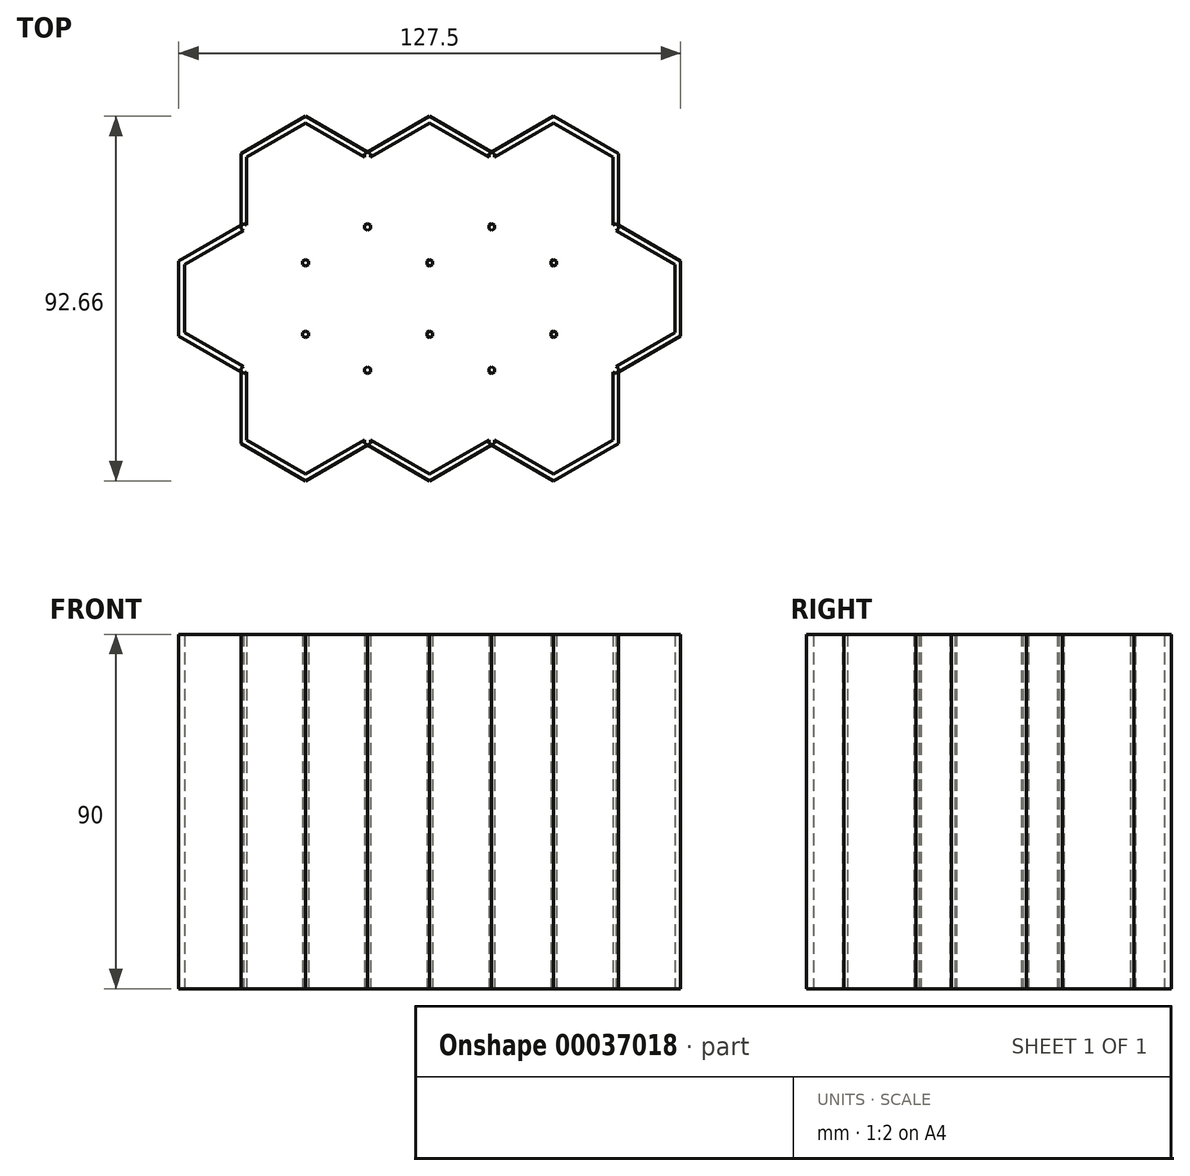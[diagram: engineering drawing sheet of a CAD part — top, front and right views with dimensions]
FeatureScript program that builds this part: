
annotation { "Feature Type Name" : "Feature", "Feature Type Description" : "" }
export const myFeature = defineFeature(function(context is Context, id is Id, definition is map)
    precondition{}
    {
        {
            var Q0;
            Q0=qCreatedBy(makeId("Top.planeOp"),FACE);
            var sketch = newSketch(context, id + "F0", { "sketchPlane" : qUnion([Q0])});
            skCircle(sketch, "E0.cCircle", {"center": v(0, 0) * mm, "radius": 15 * mm, "construction": true});
            skLineSegment(sketch, "E0.0", {"start": v(0, 17.32) * mm, "end": v(15, 8.66) * mm});
            skLineSegment(sketch, "E0.1", {"start": v(15, 8.66) * mm, "end": v(15, -8.66) * mm});
            skLineSegment(sketch, "E0.2", {"start": v(15, -8.66) * mm, "end": v(0, -17.32) * mm});
            skLineSegment(sketch, "E0.3", {"start": v(0, -17.32) * mm, "end": v(-15, -8.66) * mm});
            skLineSegment(sketch, "E0.4", {"start": v(-15, -8.66) * mm, "end": v(-15, 8.66) * mm});
            skLineSegment(sketch, "E0.5", {"start": v(-15, 8.66) * mm, "end": v(0, 17.32) * mm});
            skPoint(sketch, "E0.0.midPoint", {"position": v(7.5, 13) * mm});
            skLineSegment(sketch, "E1.0", {"start": v(-16.5, 9.53) * mm, "end": v(0, 19.05) * mm});
            skLineSegment(sketch, "E1.1", {"start": v(-16.5, -9.53) * mm, "end": v(-16.5, 9.53) * mm});
            skLineSegment(sketch, "E1.2", {"start": v(0, -19.05) * mm, "end": v(-16.5, -9.53) * mm});
            skLineSegment(sketch, "E1.3", {"start": v(16.5, -9.53) * mm, "end": v(0, -19.05) * mm});
            skLineSegment(sketch, "E1.4", {"start": v(16.5, 9.53) * mm, "end": v(16.5, -9.53) * mm});
            skLineSegment(sketch, "E1.5", {"start": v(0, 19.05) * mm, "end": v(16.5, 9.53) * mm});
            skCircle(sketch, "E2.1.0.0", {"center": v(31.5, 0) * mm, "radius": 15 * mm, "construction": true});
            skLineSegment(sketch, "E2.1.0.1", {"start": v(46.5, 8.66) * mm, "end": v(46.5, -8.66) * mm});
            skLineSegment(sketch, "E2.1.0.2", {"start": v(46.5, -8.66) * mm, "end": v(31.5, -17.32) * mm});
            skPoint(sketch, "E2.1.0.3", {"position": v(39, 13) * mm});
            skLineSegment(sketch, "E2.1.0.4", {"start": v(31.5, -19.05) * mm, "end": v(15, -9.53) * mm});
            skLineSegment(sketch, "E2.1.0.5", {"start": v(31.5, -17.32) * mm, "end": v(16.5, -8.66) * mm});
            skLineSegment(sketch, "E2.1.0.6", {"start": v(16.5, -8.66) * mm, "end": v(16.5, 8.66) * mm});
            skLineSegment(sketch, "E2.1.0.7", {"start": v(15, 9.53) * mm, "end": v(31.5, 19.05) * mm});
            skLineSegment(sketch, "E2.1.0.8", {"start": v(15, -9.53) * mm, "end": v(15, 9.53) * mm});
            skLineSegment(sketch, "E2.1.0.9", {"start": v(48, -9.53) * mm, "end": v(31.5, -19.05) * mm});
            skLineSegment(sketch, "E2.1.0.10", {"start": v(48, 9.53) * mm, "end": v(48, -9.53) * mm});
            skLineSegment(sketch, "E2.1.0.11", {"start": v(31.5, 19.05) * mm, "end": v(48, 9.53) * mm});
            skLineSegment(sketch, "E2.1.0.12", {"start": v(31.5, 17.32) * mm, "end": v(46.5, 8.66) * mm});
            skLineSegment(sketch, "E2.1.0.13", {"start": v(16.5, 8.66) * mm, "end": v(31.5, 17.32) * mm});
            skCircle(sketch, "E2.2.0.0", {"center": v(63, 0) * mm, "radius": 15 * mm, "construction": true});
            skLineSegment(sketch, "E2.2.0.1", {"start": v(78, 8.66) * mm, "end": v(78, -8.66) * mm});
            skLineSegment(sketch, "E2.2.0.2", {"start": v(78, -8.66) * mm, "end": v(63, -17.32) * mm});
            skPoint(sketch, "E2.2.0.3", {"position": v(70.5, 13) * mm});
            skLineSegment(sketch, "E2.2.0.4", {"start": v(63, -19.05) * mm, "end": v(46.5, -9.53) * mm});
            skLineSegment(sketch, "E2.2.0.5", {"start": v(63, -17.32) * mm, "end": v(48, -8.66) * mm});
            skLineSegment(sketch, "E2.2.0.6", {"start": v(48, -8.66) * mm, "end": v(48, 8.66) * mm});
            skLineSegment(sketch, "E2.2.0.7", {"start": v(46.5, 9.53) * mm, "end": v(63, 19.05) * mm});
            skLineSegment(sketch, "E2.2.0.8", {"start": v(46.5, -9.53) * mm, "end": v(46.5, 9.53) * mm});
            skLineSegment(sketch, "E2.2.0.9", {"start": v(79.5, -9.53) * mm, "end": v(63, -19.05) * mm});
            skLineSegment(sketch, "E2.2.0.10", {"start": v(79.5, 9.53) * mm, "end": v(79.5, -9.53) * mm});
            skLineSegment(sketch, "E2.2.0.11", {"start": v(63, 19.05) * mm, "end": v(79.5, 9.53) * mm});
            skLineSegment(sketch, "E2.2.0.12", {"start": v(63, 17.32) * mm, "end": v(78, 8.66) * mm});
            skLineSegment(sketch, "E2.2.0.13", {"start": v(48, 8.66) * mm, "end": v(63, 17.32) * mm});
            skLineSegment(sketch, "E2.direction1", {"start": v(0, 0) * mm, "end": v(31.5, 0) * mm, "construction": true});
            skLineSegment(sketch, "E3.1.0.0", {"start": v(-15.75, 46.33) * mm, "end": v(0.75, 36.8) * mm});
            skLineSegment(sketch, "E3.1.0.1", {"start": v(-15.75, 27.28) * mm, "end": v(15.75, 27.28) * mm, "construction": true});
            skLineSegment(sketch, "E3.1.0.2", {"start": v(-30.75, 18.62) * mm, "end": v(-30.75, 35.94) * mm});
            skLineSegment(sketch, "E3.1.0.3", {"start": v(-15.75, 9.96) * mm, "end": v(-30.75, 18.62) * mm});
            skLineSegment(sketch, "E3.1.0.4", {"start": v(-0.75, 18.62) * mm, "end": v(-15.75, 9.96) * mm});
            skLineSegment(sketch, "E3.1.0.5", {"start": v(-0.75, 35.94) * mm, "end": v(-0.75, 18.62) * mm});
            skLineSegment(sketch, "E3.1.0.6", {"start": v(0.75, 36.8) * mm, "end": v(0.75, 17.75) * mm});
            skPoint(sketch, "E3.1.0.7", {"position": v(-8.25, 40.27) * mm});
            skLineSegment(sketch, "E3.1.0.8", {"start": v(-15.75, 44.6) * mm, "end": v(-0.75, 35.94) * mm});
            skCircle(sketch, "E3.1.0.9", {"center": v(-15.75, 27.28) * mm, "radius": 15 * mm, "construction": true});
            skLineSegment(sketch, "E3.1.0.10", {"start": v(-32.25, 17.75) * mm, "end": v(-32.25, 36.8) * mm});
            skLineSegment(sketch, "E3.1.0.11", {"start": v(-15.75, 8.23) * mm, "end": v(-32.25, 17.75) * mm});
            skLineSegment(sketch, "E3.1.0.12", {"start": v(0.75, 17.75) * mm, "end": v(-15.75, 8.23) * mm});
            skLineSegment(sketch, "E3.1.0.13", {"start": v(-30.75, 35.94) * mm, "end": v(-15.75, 44.6) * mm});
            skLineSegment(sketch, "E3.1.0.14", {"start": v(-32.25, 36.8) * mm, "end": v(-15.75, 46.33) * mm});
            skLineSegment(sketch, "E3.direction1", {"start": v(0, 0) * mm, "end": v(-15.75, 27.28) * mm, "construction": true});
            skLineSegment(sketch, "E4.1.0.0", {"start": v(0.75, 35.94) * mm, "end": v(15.75, 44.6) * mm});
            skLineSegment(sketch, "E4.1.0.1", {"start": v(30.75, 35.94) * mm, "end": v(30.75, 18.62) * mm});
            skLineSegment(sketch, "E4.1.0.2", {"start": v(15.75, 8.23) * mm, "end": v(-0.75, 17.75) * mm});
            skLineSegment(sketch, "E4.1.0.3", {"start": v(0.75, 18.62) * mm, "end": v(0.75, 35.94) * mm});
            skLineSegment(sketch, "E4.1.0.4", {"start": v(32.25, 36.8) * mm, "end": v(32.25, 17.75) * mm});
            skLineSegment(sketch, "E4.1.0.5", {"start": v(-0.75, 36.8) * mm, "end": v(15.75, 46.33) * mm});
            skPoint(sketch, "E4.1.0.6", {"position": v(23.25, 40.27) * mm});
            skLineSegment(sketch, "E4.1.0.7", {"start": v(32.25, 17.75) * mm, "end": v(15.75, 8.23) * mm});
            skCircle(sketch, "E4.1.0.8", {"center": v(15.75, 27.28) * mm, "radius": 15 * mm, "construction": true});
            skLineSegment(sketch, "E4.1.0.9", {"start": v(-0.75, 17.75) * mm, "end": v(-0.75, 36.8) * mm});
            skLineSegment(sketch, "E4.1.0.10", {"start": v(30.75, 18.62) * mm, "end": v(15.75, 9.96) * mm});
            skLineSegment(sketch, "E4.1.0.11", {"start": v(15.75, 46.33) * mm, "end": v(32.25, 36.8) * mm});
            skLineSegment(sketch, "E4.1.0.12", {"start": v(15.75, 9.96) * mm, "end": v(0.75, 18.62) * mm});
            skLineSegment(sketch, "E4.1.0.13", {"start": v(15.75, 44.6) * mm, "end": v(30.75, 35.94) * mm});
            skLineSegment(sketch, "E4.2.0.0", {"start": v(32.25, 35.94) * mm, "end": v(47.25, 44.6) * mm});
            skLineSegment(sketch, "E4.2.0.1", {"start": v(62.25, 35.94) * mm, "end": v(62.25, 18.62) * mm});
            skLineSegment(sketch, "E4.2.0.2", {"start": v(47.25, 8.23) * mm, "end": v(30.75, 17.75) * mm});
            skLineSegment(sketch, "E4.2.0.3", {"start": v(32.25, 18.62) * mm, "end": v(32.25, 35.94) * mm});
            skLineSegment(sketch, "E4.2.0.4", {"start": v(63.75, 36.8) * mm, "end": v(63.75, 17.75) * mm});
            skLineSegment(sketch, "E4.2.0.5", {"start": v(30.75, 36.8) * mm, "end": v(47.25, 46.33) * mm});
            skPoint(sketch, "E4.2.0.6", {"position": v(54.75, 40.27) * mm});
            skLineSegment(sketch, "E4.2.0.7", {"start": v(63.75, 17.75) * mm, "end": v(47.25, 8.23) * mm});
            skCircle(sketch, "E4.2.0.8", {"center": v(47.25, 27.28) * mm, "radius": 15 * mm, "construction": true});
            skLineSegment(sketch, "E4.2.0.9", {"start": v(30.75, 17.75) * mm, "end": v(30.75, 36.8) * mm});
            skLineSegment(sketch, "E4.2.0.10", {"start": v(62.25, 18.62) * mm, "end": v(47.25, 9.96) * mm});
            skLineSegment(sketch, "E4.2.0.11", {"start": v(47.25, 46.33) * mm, "end": v(63.75, 36.8) * mm});
            skLineSegment(sketch, "E4.2.0.12", {"start": v(47.25, 9.96) * mm, "end": v(32.25, 18.62) * mm});
            skLineSegment(sketch, "E4.2.0.13", {"start": v(47.25, 44.6) * mm, "end": v(62.25, 35.94) * mm});
            skLineSegment(sketch, "E4.3.0.0", {"start": v(63.75, 35.94) * mm, "end": v(78.75, 44.6) * mm});
            skLineSegment(sketch, "E4.3.0.1", {"start": v(93.75, 35.94) * mm, "end": v(93.75, 18.62) * mm});
            skLineSegment(sketch, "E4.3.0.2", {"start": v(78.75, 8.23) * mm, "end": v(62.25, 17.75) * mm});
            skLineSegment(sketch, "E4.3.0.3", {"start": v(63.75, 18.62) * mm, "end": v(63.75, 35.94) * mm});
            skLineSegment(sketch, "E4.3.0.4", {"start": v(95.25, 36.8) * mm, "end": v(95.25, 17.75) * mm});
            skLineSegment(sketch, "E4.3.0.5", {"start": v(62.25, 36.8) * mm, "end": v(78.75, 46.33) * mm});
            skPoint(sketch, "E4.3.0.6", {"position": v(86.25, 40.27) * mm});
            skLineSegment(sketch, "E4.3.0.7", {"start": v(95.25, 17.75) * mm, "end": v(78.75, 8.23) * mm});
            skCircle(sketch, "E4.3.0.8", {"center": v(78.75, 27.28) * mm, "radius": 15 * mm, "construction": true});
            skLineSegment(sketch, "E4.3.0.9", {"start": v(62.25, 17.75) * mm, "end": v(62.25, 36.8) * mm});
            skLineSegment(sketch, "E4.3.0.10", {"start": v(93.75, 18.62) * mm, "end": v(78.75, 9.96) * mm});
            skLineSegment(sketch, "E4.3.0.11", {"start": v(78.75, 46.33) * mm, "end": v(95.25, 36.8) * mm});
            skLineSegment(sketch, "E4.3.0.12", {"start": v(78.75, 9.96) * mm, "end": v(63.75, 18.62) * mm});
            skLineSegment(sketch, "E4.3.0.13", {"start": v(78.75, 44.6) * mm, "end": v(93.75, 35.94) * mm});
            skLineSegment(sketch, "E5.1.0.0", {"start": v(-15, 45.9) * mm, "end": v(-15, 63.22) * mm});
            skLineSegment(sketch, "E5.1.0.1", {"start": v(78, 45.9) * mm, "end": v(63, 37.24) * mm});
            skLineSegment(sketch, "E5.1.0.2", {"start": v(0, 37.24) * mm, "end": v(-15, 45.9) * mm});
            skLineSegment(sketch, "E5.1.0.3", {"start": v(48, 64.09) * mm, "end": v(48, 45.03) * mm});
            skLineSegment(sketch, "E5.1.0.4", {"start": v(79.5, 45.03) * mm, "end": v(63, 35.5) * mm});
            skLineSegment(sketch, "E5.1.0.5", {"start": v(79.5, 64.09) * mm, "end": v(79.5, 45.03) * mm});
            skPoint(sketch, "E5.1.0.6", {"position": v(7.5, 67.55) * mm});
            skLineSegment(sketch, "E5.1.0.7", {"start": v(-15, 63.22) * mm, "end": v(0, 71.88) * mm});
            skLineSegment(sketch, "E5.1.0.8", {"start": v(0, 73.61) * mm, "end": v(16.5, 64.09) * mm});
            skLineSegment(sketch, "E5.1.0.9", {"start": v(15, 63.22) * mm, "end": v(15, 45.9) * mm});
            skLineSegment(sketch, "E5.1.0.10", {"start": v(48, 45.03) * mm, "end": v(31.5, 35.5) * mm});
            skLineSegment(sketch, "E5.1.0.11", {"start": v(48, 45.9) * mm, "end": v(48, 63.22) * mm});
            skLineSegment(sketch, "E5.1.0.12", {"start": v(46.5, 63.22) * mm, "end": v(46.5, 45.9) * mm});
            skCircle(sketch, "E5.1.0.13", {"center": v(63, 54.56) * mm, "radius": 15 * mm, "construction": true});
            skLineSegment(sketch, "E5.1.0.14", {"start": v(16.5, 63.22) * mm, "end": v(31.5, 71.88) * mm});
            skLineSegment(sketch, "E5.1.0.15", {"start": v(0, 71.88) * mm, "end": v(15, 63.22) * mm});
            skPoint(sketch, "E5.1.0.16", {"position": v(39, 67.55) * mm});
            skLineSegment(sketch, "E5.1.0.17", {"start": v(63, 35.5) * mm, "end": v(46.5, 45.03) * mm});
            skLineSegment(sketch, "E5.1.0.18", {"start": v(63, 37.24) * mm, "end": v(48, 45.9) * mm});
            skLineSegment(sketch, "E5.1.0.19", {"start": v(15, 45.03) * mm, "end": v(15, 64.09) * mm});
            skLineSegment(sketch, "E5.1.0.20", {"start": v(15, 64.09) * mm, "end": v(31.5, 73.61) * mm});
            skLineSegment(sketch, "E5.1.0.21", {"start": v(31.5, 73.61) * mm, "end": v(48, 64.09) * mm});
            skLineSegment(sketch, "E5.1.0.22", {"start": v(-16.5, 45.03) * mm, "end": v(-16.5, 64.09) * mm});
            skLineSegment(sketch, "E5.1.0.23", {"start": v(46.5, 45.03) * mm, "end": v(46.5, 64.09) * mm});
            skLineSegment(sketch, "E5.1.0.24", {"start": v(63, 73.61) * mm, "end": v(79.5, 64.09) * mm});
            skLineSegment(sketch, "E5.1.0.25", {"start": v(48, 63.22) * mm, "end": v(63, 71.88) * mm});
            skLineSegment(sketch, "E5.1.0.26", {"start": v(31.5, 35.5) * mm, "end": v(15, 45.03) * mm});
            skCircle(sketch, "E5.1.0.27", {"center": v(0, 54.56) * mm, "radius": 15 * mm, "construction": true});
            skLineSegment(sketch, "E5.1.0.28", {"start": v(0, 54.56) * mm, "end": v(31.5, 54.56) * mm, "construction": true});
            skLineSegment(sketch, "E5.1.0.29", {"start": v(46.5, 64.09) * mm, "end": v(63, 73.61) * mm});
            skLineSegment(sketch, "E5.1.0.30", {"start": v(31.5, 37.24) * mm, "end": v(16.5, 45.9) * mm});
            skLineSegment(sketch, "E5.1.0.31", {"start": v(0, 35.5) * mm, "end": v(-16.5, 45.03) * mm});
            skLineSegment(sketch, "E5.1.0.32", {"start": v(15, 45.9) * mm, "end": v(0, 37.24) * mm});
            skCircle(sketch, "E5.1.0.33", {"center": v(31.5, 54.56) * mm, "radius": 15 * mm, "construction": true});
            skLineSegment(sketch, "E5.1.0.34", {"start": v(78, 63.22) * mm, "end": v(78, 45.9) * mm});
            skLineSegment(sketch, "E5.1.0.35", {"start": v(16.5, 64.09) * mm, "end": v(16.5, 45.03) * mm});
            skLineSegment(sketch, "E5.1.0.36", {"start": v(16.5, 45.03) * mm, "end": v(0, 35.5) * mm});
            skLineSegment(sketch, "E5.1.0.37", {"start": v(-16.5, 64.09) * mm, "end": v(0, 73.61) * mm});
            skLineSegment(sketch, "E5.1.0.38", {"start": v(16.5, 45.9) * mm, "end": v(16.5, 63.22) * mm});
            skLineSegment(sketch, "E5.1.0.39", {"start": v(46.5, 45.9) * mm, "end": v(31.5, 37.24) * mm});
            skLineSegment(sketch, "E5.1.0.40", {"start": v(0, 54.56) * mm, "end": v(31.5, 54.56) * mm, "construction": true});
            skPoint(sketch, "E5.1.0.41", {"position": v(70.5, 67.55) * mm});
            skLineSegment(sketch, "E5.1.0.42", {"start": v(31.5, 71.88) * mm, "end": v(46.5, 63.22) * mm});
            skLineSegment(sketch, "E5.1.0.43", {"start": v(63, 71.88) * mm, "end": v(78, 63.22) * mm});
            skLineSegment(sketch, "E5.direction1", {"start": v(-15.75, 27.28) * mm, "end": v(0, 54.56) * mm, "construction": true});
            skSolve(sketch);
        }
        {
            assignVariable(context, id + "F1", {"name" : "Height", "anyValue" : 90});
        }
        {
            var Q0;
            {var subQ2=sQuery(id+"F0.wireOp",EDGE,"E5.1.0.14");Q0=makeQuery(id+"F0.imprint","IMPRINT",FACE,{"disambiguationData":[TD([[makeQuery(id+"F0.imprint","IMPRINT",EDGE,{"derivedFrom":subQ2}),1.0]])]});}
            var Q1;
            {var subQ10=sQuery(id+"F0.wireOp",EDGE,"E5.1.0.0");Q1=makeQuery(id+"F0.imprint","IMPRINT",FACE,{"disambiguationData":[TD([[makeQuery(id+"F0.imprint","IMPRINT",EDGE,{"derivedFrom":subQ10}),1.0]])]});}
            var Q2;
            Q2=makeQuery(id+"F0.imprint","IMPRINT",FACE,{"disambiguationData":[TD([[makeQuery(id+"F0.imprint","IMPRINT",EDGE,{"derivedFrom":sQuery(id+"F0.wireOp",EDGE,"E4.3.0.1")}),1.0]])]});
            var Q3;
            {var subQ5=sQuery(id+"F0.wireOp",EDGE,"E2.2.0.1");Q3=makeQuery(id+"F0.imprint","IMPRINT",FACE,{"disambiguationData":[TD([[makeQuery(id+"F0.imprint","IMPRINT",EDGE,{"derivedFrom":subQ5}),1.0]])]});}
            var Q4;
            {var subQ3=sQuery(id+"F0.wireOp",EDGE,"E2.1.0.2");Q4=makeQuery(id+"F0.imprint","IMPRINT",FACE,{"disambiguationData":[TD([[makeQuery(id+"F0.imprint","IMPRINT",EDGE,{"derivedFrom":subQ3}),1.0]])]});}
            var Q5;
            Q5=makeQuery(id+"F0.imprint","IMPRINT",FACE,{"disambiguationData":[TD([[makeQuery(id+"F0.imprint","IMPRINT",EDGE,{"derivedFrom":sQuery(id+"F0.wireOp",EDGE,"E3.1.0.2")}),1.0]])]});
            var Q6;
            {var subQ9=sQuery(id+"F0.wireOp",EDGE,"E0.2");Q6=makeQuery(id+"F0.imprint","IMPRINT",FACE,{"disambiguationData":[TD([[makeQuery(id+"F0.imprint","IMPRINT",EDGE,{"derivedFrom":subQ9}),1.0]])]});}
            var Q7;
            {var subQ4=sQuery(id+"F0.wireOp",EDGE,"E2.1.0.6");Q7=makeQuery(id+"F0.imprint","IMPRINT",FACE,{"disambiguationData":[TD([[makeQuery(id+"F0.imprint","IMPRINT",EDGE,{"derivedFrom":subQ4}),1.0]])]});}
            var Q8;
            {var subQ4=sQuery(id+"F0.wireOp",EDGE,"E5.1.0.24");Q8=makeQuery(id+"F0.imprint","IMPRINT",FACE,{"disambiguationData":[TD([[makeQuery(id+"F0.imprint","IMPRINT",EDGE,{"derivedFrom":subQ4}),-1.0]])]});}
            var Q9;
            {var subQ0=sQuery(id+"F0.wireOp",EDGE,"E4.2.0.12");Q9=makeQuery(id+"F0.imprint","IMPRINT",FACE,{"disambiguationData":[TD([[makeQuery(id+"F0.imprint","IMPRINT",EDGE,{"derivedFrom":subQ0}),1.0]])]});}
            var Q10;
            {var subQ0=sQuery(id+"F0.wireOp",EDGE,"E5.1.0.38");Q10=makeQuery(id+"F0.imprint","IMPRINT",FACE,{"disambiguationData":[TD([[makeQuery(id+"F0.imprint","IMPRINT",EDGE,{"derivedFrom":subQ0}),1.0]])]});}
            var Q11;
            {var subQ8=sQuery(id+"F0.wireOp",EDGE,"E5.1.0.2");Q11=makeQuery(id+"F0.imprint","IMPRINT",FACE,{"disambiguationData":[TD([[makeQuery(id+"F0.imprint","IMPRINT",EDGE,{"derivedFrom":subQ8}),1.0]])]});}
            var Q12;
            {var subQ4=sQuery(id+"F0.wireOp",EDGE,"E4.2.0.10");Q12=makeQuery(id+"F0.imprint","IMPRINT",FACE,{"disambiguationData":[TD([[makeQuery(id+"F0.imprint","IMPRINT",EDGE,{"derivedFrom":subQ4}),1.0]])]});}
            var Q13;
            {var subQ0=sQuery(id+"F0.wireOp",EDGE,"E4.3.0.12");Q13=makeQuery(id+"F0.imprint","IMPRINT",FACE,{"disambiguationData":[TD([[makeQuery(id+"F0.imprint","IMPRINT",EDGE,{"derivedFrom":subQ0}),1.0]])]});}
            var Q14;
            {var subQ6=sQuery(id+"F0.wireOp",EDGE,"E4.2.0.3");Q14=makeQuery(id+"F0.imprint","IMPRINT",FACE,{"disambiguationData":[TD([[makeQuery(id+"F0.imprint","IMPRINT",EDGE,{"derivedFrom":subQ6}),1.0]])]});}
            var Q15;
            {var subQ8=sQuery(id+"F0.wireOp",EDGE,"E2.2.0.6");Q15=makeQuery(id+"F0.imprint","IMPRINT",FACE,{"disambiguationData":[TD([[makeQuery(id+"F0.imprint","IMPRINT",EDGE,{"derivedFrom":subQ8}),1.0]])]});}
            var Q16;
            {var subQ0=sQuery(id+"F0.wireOp",EDGE,"E4.1.0.12");Q16=makeQuery(id+"F0.imprint","IMPRINT",FACE,{"disambiguationData":[TD([[makeQuery(id+"F0.imprint","IMPRINT",EDGE,{"derivedFrom":subQ0}),1.0]])]});}
            var Q17;
            {var subQ4=sQuery(id+"F0.wireOp",EDGE,"E4.1.0.10");Q17=makeQuery(id+"F0.imprint","IMPRINT",FACE,{"disambiguationData":[TD([[makeQuery(id+"F0.imprint","IMPRINT",EDGE,{"derivedFrom":subQ4}),1.0]])]});}
            var Q18;
            {var subQ4=sQuery(id+"F0.wireOp",EDGE,"E3.1.0.4");Q18=makeQuery(id+"F0.imprint","IMPRINT",FACE,{"disambiguationData":[TD([[makeQuery(id+"F0.imprint","IMPRINT",EDGE,{"derivedFrom":subQ4}),1.0]])]});}
            var Q19;
            {var subQ4=sQuery(id+"F0.wireOp",EDGE,"E4.1.0.3");Q19=makeQuery(id+"F0.imprint","IMPRINT",FACE,{"disambiguationData":[TD([[makeQuery(id+"F0.imprint","IMPRINT",EDGE,{"derivedFrom":subQ4}),1.0]])]});}
            var Q20;
            {var subQ0=sQuery(id+"F0.wireOp",EDGE,"E5.1.0.18");Q20=makeQuery(id+"F0.imprint","IMPRINT",FACE,{"disambiguationData":[TD([[makeQuery(id+"F0.imprint","IMPRINT",EDGE,{"derivedFrom":subQ0}),1.0]])]});}
            var Q21;
            {var subQ6=sQuery(id+"F0.wireOp",EDGE,"E5.1.0.30");Q21=makeQuery(id+"F0.imprint","IMPRINT",FACE,{"disambiguationData":[TD([[makeQuery(id+"F0.imprint","IMPRINT",EDGE,{"derivedFrom":subQ6}),1.0]])]});}
            var Q22;
            {var subQ5=sQuery(id+"F0.wireOp",EDGE,"E5.1.0.32");Q22=makeQuery(id+"F0.imprint","IMPRINT",FACE,{"disambiguationData":[TD([[makeQuery(id+"F0.imprint","IMPRINT",EDGE,{"derivedFrom":subQ5}),1.0]])]});}
            var Q23;
            {var subQ10=sQuery(id+"F0.wireOp",EDGE,"E5.1.0.11");Q23=makeQuery(id+"F0.imprint","IMPRINT",FACE,{"disambiguationData":[TD([[makeQuery(id+"F0.imprint","IMPRINT",EDGE,{"derivedFrom":subQ10}),1.0]])]});}
            var Q24;
            {var subQ0=sQuery(id+"F0.wireOp",EDGE,"E5.1.0.39");Q24=makeQuery(id+"F0.imprint","IMPRINT",FACE,{"disambiguationData":[TD([[makeQuery(id+"F0.imprint","IMPRINT",EDGE,{"derivedFrom":subQ0}),1.0]])]});}
            var Q25;
            {var subQ6=sQuery(id+"F0.wireOp",EDGE,"E4.3.0.3");Q25=makeQuery(id+"F0.imprint","IMPRINT",FACE,{"disambiguationData":[TD([[makeQuery(id+"F0.imprint","IMPRINT",EDGE,{"derivedFrom":subQ6}),1.0]])]});}
            var Q26;
            {var subQ8=sQuery(id+"F0.wireOp",EDGE,"E5.1.0.1");Q26=makeQuery(id+"F0.imprint","IMPRINT",FACE,{"disambiguationData":[TD([[makeQuery(id+"F0.imprint","IMPRINT",EDGE,{"derivedFrom":subQ8}),1.0]])]});}
            var Q27;
            {var subQ1=sQuery(id+"F0.wireOp",EDGE,"E4.2.0.9");var subQ7=sQuery(id+"F0.wireOp",EDGE,"E4.2.0.5");var subQ8=makeQuery(id+"F0.imprint","INTERSECT",VERTEX,{"derivedFrom":[subQ7,subQ1]});Q27=makeQuery(id+"F0.imprint","IMPRINT",FACE,{"disambiguationData":[TD([[makeQuery(id+"F0.imprint","IMPRINT",EDGE,{"disambiguationData":[TD([[subQ8,1.0]])],"derivedFrom":subQ1}),-1.0]])]});}
            var Q28;
            {var subQ1=sQuery(id+"F0.wireOp",EDGE,"E2.1.0.8");var subQ5=sQuery(id+"F0.wireOp",EDGE,"E2.1.0.7");var subQ6=makeQuery(id+"F0.imprint","INTERSECT",VERTEX,{"derivedFrom":[subQ5,subQ1]});Q28=makeQuery(id+"F0.imprint","IMPRINT",FACE,{"disambiguationData":[TD([[makeQuery(id+"F0.imprint","IMPRINT",EDGE,{"disambiguationData":[TD([[subQ6,1.0]])],"derivedFrom":subQ1}),-1.0]])]});}
            var Q29;
            {var subQ5=sQuery(id+"F0.wireOp",EDGE,"E5.1.0.10");var subQ7=sQuery(id+"F0.wireOp",EDGE,"E5.1.0.3");var subQ8=makeQuery(id+"F0.imprint","INTERSECT",VERTEX,{"derivedFrom":[subQ7,subQ5]});Q29=makeQuery(id+"F0.imprint","IMPRINT",FACE,{"disambiguationData":[TD([[makeQuery(id+"F0.imprint","IMPRINT",EDGE,{"disambiguationData":[TD([[subQ8,-1.0]])],"derivedFrom":subQ5}),-1.0]])]});}
            var Q30;
            {var subQ5=sQuery(id+"F0.wireOp",EDGE,"E4.1.0.9");var subQ7=sQuery(id+"F0.wireOp",EDGE,"E4.1.0.5");var subQ8=makeQuery(id+"F0.imprint","INTERSECT",VERTEX,{"derivedFrom":[subQ7,subQ5]});Q30=makeQuery(id+"F0.imprint","IMPRINT",FACE,{"disambiguationData":[TD([[makeQuery(id+"F0.imprint","IMPRINT",EDGE,{"disambiguationData":[TD([[subQ8,1.0]])],"derivedFrom":subQ5}),-1.0]])]});}
            var Q31;
            {var subQ5=sQuery(id+"F0.wireOp",EDGE,"E4.2.0.7");var subQ7=sQuery(id+"F0.wireOp",EDGE,"E4.2.0.4");var subQ8=makeQuery(id+"F0.imprint","INTERSECT",VERTEX,{"derivedFrom":[subQ7,subQ5]});Q31=makeQuery(id+"F0.imprint","IMPRINT",FACE,{"disambiguationData":[TD([[makeQuery(id+"F0.imprint","IMPRINT",EDGE,{"disambiguationData":[TD([[subQ8,-1.0]])],"derivedFrom":subQ5}),-1.0]])]});}
            var Q32;
            {var subQ5=sQuery(id+"F0.wireOp",EDGE,"E3.1.0.12");var subQ7=sQuery(id+"F0.wireOp",EDGE,"E3.1.0.6");var subQ8=makeQuery(id+"F0.imprint","INTERSECT",VERTEX,{"derivedFrom":[subQ7,subQ5]});Q32=makeQuery(id+"F0.imprint","IMPRINT",FACE,{"disambiguationData":[TD([[makeQuery(id+"F0.imprint","IMPRINT",EDGE,{"disambiguationData":[TD([[subQ8,-1.0]])],"derivedFrom":subQ5}),-1.0]])]});}
            var Q33;
            {var subQ1=sQuery(id+"F0.wireOp",EDGE,"E4.3.0.9");var subQ7=sQuery(id+"F0.wireOp",EDGE,"E4.3.0.5");var subQ8=makeQuery(id+"F0.imprint","INTERSECT",VERTEX,{"derivedFrom":[subQ7,subQ1]});Q33=makeQuery(id+"F0.imprint","IMPRINT",FACE,{"disambiguationData":[TD([[makeQuery(id+"F0.imprint","IMPRINT",EDGE,{"disambiguationData":[TD([[subQ8,1.0]])],"derivedFrom":subQ1}),-1.0]])]});}
            var Q34;
            {var subQ1=sQuery(id+"F0.wireOp",EDGE,"E5.1.0.26");var subQ7=sQuery(id+"F0.wireOp",EDGE,"E5.1.0.19");var subQ8=makeQuery(id+"F0.imprint","INTERSECT",VERTEX,{"derivedFrom":[subQ7,subQ1]});Q34=makeQuery(id+"F0.imprint","IMPRINT",FACE,{"disambiguationData":[TD([[makeQuery(id+"F0.imprint","IMPRINT",EDGE,{"disambiguationData":[TD([[subQ8,1.0]])],"derivedFrom":subQ1}),-1.0]])]});}
            var Q35;
            {var subQ5=sQuery(id+"F0.wireOp",EDGE,"E2.2.0.8");var subQ7=sQuery(id+"F0.wireOp",EDGE,"E2.2.0.7");var subQ8=makeQuery(id+"F0.imprint","INTERSECT",VERTEX,{"derivedFrom":[subQ7,subQ5]});Q35=makeQuery(id+"F0.imprint","IMPRINT",FACE,{"disambiguationData":[TD([[makeQuery(id+"F0.imprint","IMPRINT",EDGE,{"disambiguationData":[TD([[subQ8,1.0]])],"derivedFrom":subQ5}),-1.0]])]});}
            var Q36;
            {var subQ5=sQuery(id+"F0.wireOp",EDGE,"E4.1.0.7");var subQ7=sQuery(id+"F0.wireOp",EDGE,"E4.1.0.4");var subQ8=makeQuery(id+"F0.imprint","INTERSECT",VERTEX,{"derivedFrom":[subQ7,subQ5]});Q36=makeQuery(id+"F0.imprint","IMPRINT",FACE,{"disambiguationData":[TD([[makeQuery(id+"F0.imprint","IMPRINT",EDGE,{"disambiguationData":[TD([[subQ8,-1.0]])],"derivedFrom":subQ5}),-1.0]])]});}
            extrude(context, id + "F2", {"entities" : qUnion([Q0, Q1, Q2, Q3, Q4, Q5, Q6, Q7, Q8, Q9, Q10, Q11, Q12, Q13, Q14, Q15, Q16, Q17, Q18, Q19, Q20, Q21, Q22, Q23, Q24, Q25, Q26, Q27, Q28, Q29, Q30, Q31, Q32, Q33, Q34, Q35, Q36]), "depth" : (getVariable(context, 'Height')) * mm});
        }
    });
